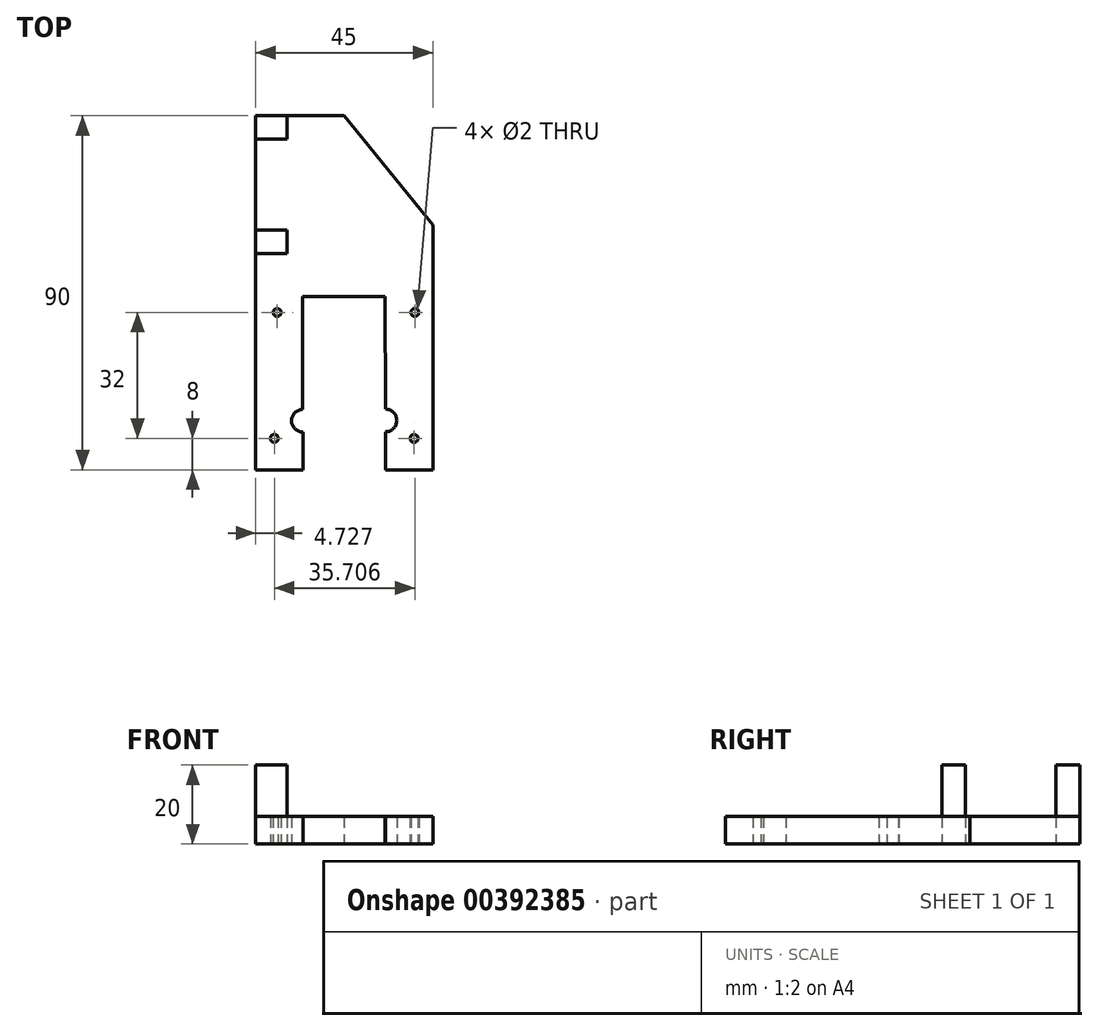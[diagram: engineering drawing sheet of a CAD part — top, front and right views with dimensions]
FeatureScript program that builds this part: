
annotation { "Feature Type Name" : "Feature", "Feature Type Description" : "" }
export const myFeature = defineFeature(function(context is Context, id is Id, definition is map)
    precondition{}
    {
        {
            var Q0;
            Q0=qCreatedBy(makeId("Top.planeOp"),FACE);
            var sketch = newSketch(context, id + "F0", { "sketchPlane" : qUnion([Q0])});
            skLineSegment(sketch, "E0.bottom", {"start": v(22.5, -45) * mm, "end": v(10.5, -45) * mm});
            skLineSegment(sketch, "E0.top", {"start": v(22.5, 45) * mm, "end": v(-22.5, 45) * mm});
            skLineSegment(sketch, "E0.left", {"start": v(22.5, -45) * mm, "end": v(22.5, 45) * mm});
            skLineSegment(sketch, "E0.right", {"start": v(-22.5, -45) * mm, "end": v(-22.5, 45) * mm});
            skPoint(sketch, "E0.middle", {"position": v(0, 0) * mm});
            skLineSegment(sketch, "E1.bottom", {"start": v(-10.63, -1) * mm, "end": v(10.37, -0.94) * mm});
            skLineSegment(sketch, "E1.left", {"start": v(-10.63, -1) * mm, "end": v(-10.5, -45) * mm});
            skLineSegment(sketch, "E1.right", {"start": v(10.37, -0.94) * mm, "end": v(10.5, -45) * mm});
            skLineSegment(sketch, "E2.bottom", {"start": v(-22.5, 39) * mm, "end": v(-14.5, 39) * mm});
            skLineSegment(sketch, "E2.top", {"start": v(-22.5, 45) * mm, "end": v(-14.5, 45) * mm});
            skLineSegment(sketch, "E2.left", {"start": v(-22.5, 39) * mm, "end": v(-22.5, 45) * mm});
            skLineSegment(sketch, "E2.right", {"start": v(-14.5, 39) * mm, "end": v(-14.5, 45) * mm});
            skLineSegment(sketch, "E3.bottom", {"start": v(-22.5, 16) * mm, "end": v(-14.5, 16) * mm});
            skLineSegment(sketch, "E3.top", {"start": v(-22.5, 10) * mm, "end": v(-14.5, 10) * mm});
            skLineSegment(sketch, "E3.left", {"start": v(-22.5, 16) * mm, "end": v(-22.5, 10) * mm});
            skLineSegment(sketch, "E3.right", {"start": v(-14.5, 16) * mm, "end": v(-14.5, 10) * mm});
            skLineSegment(sketch, "E4.trimOffspring", {"start": v(-10.5, -45) * mm, "end": v(-22.5, -45) * mm});
            skPoint(sketch, "E5", {"position": v(-17.77, -37) * mm});
            skPoint(sketch, "E6", {"position": v(-17.07, -5) * mm});
            skPoint(sketch, "E7", {"position": v(17.93, -5) * mm});
            skPoint(sketch, "E8", {"position": v(17.73, -37) * mm});
            skPoint(sketch, "E9.positionSnap0", {"position": v(-18.5, 45) * mm});
            skPoint(sketch, "E10.positionSnap0", {"position": v(-18.5, 16) * mm});
            skPoint(sketch, "E11", {"position": v(-10.54, -32.5) * mm});
            skPoint(sketch, "E12", {"position": v(0, 45) * mm});
            skPoint(sketch, "E13", {"position": v(22.5, 17.15) * mm});
            skLineSegment(sketch, "E14", {"start": v(0, 45) * mm, "end": v(22.5, 17.15) * mm});
            skPoint(sketch, "E15", {"position": v(10.46, -32.44) * mm});
            skLineSegment(sketch, "E16", {"start": v(0, -64.42) * mm, "end": v(0, 71.46) * mm, "construction": true});
            skSolve(sketch);
        }
        {
            var Q0;
            Q0=makeQuery(id+"F0.imprint","IMPRINT",FACE,{"disambiguationData":[TD([[makeQuery(id+"F0.imprint","IMPRINT",EDGE,{"derivedFrom":sQuery(id+"F0.wireOp",EDGE,"E2.bottom")}),1.0]])]});
            extrude(context, id + "F1", {"entities" : qUnion([Q0]), "depth" : 20 * mm});
        }
        {
            var Q0;
            Q0=makeQuery(id+"F0.imprint","IMPRINT",FACE,{"disambiguationData":[TD([[makeQuery(id+"F0.imprint","IMPRINT",EDGE,{"derivedFrom":sQuery(id+"F0.wireOp",EDGE,"E3.bottom")}),-1.0]])]});
            extrude(context, id + "F2", {"entities" : qUnion([Q0]), "depth" : 20 * mm});
        }
        {
            var Q0;
            Q0=makeQuery(id+"F0.imprint","IMPRINT",FACE,{"disambiguationData":[TD([[makeQuery(id+"F0.imprint","IMPRINT",EDGE,{"derivedFrom":sQuery(id+"F0.wireOp",EDGE,"E0.bottom")}),-1.0]])]});
            extrude(context, id + "F3", {"entities" : qUnion([Q0]), "depth" : 7 * mm});
        }
        {
            var Q0;
            Q0=sQuery(id+"F0.wireOp",VERTEX,"E6");
            var Q1;
            Q1=sQuery(id+"F0.wireOp",VERTEX,"E5");
            var Q2;
            Q2=sQuery(id+"F0.wireOp",VERTEX,"E8");
            var Q3;
            Q3=sQuery(id+"F0.wireOp",VERTEX,"E7");
            var Q4;
            Q4=makeQuery(id+"F3.opExtrude","SWEPT_BODY",BODY,{"disambiguationData":[OSD([sQuery(id+"F0.wireOp",EDGE,"E0.bottom"),sQuery(id+"F0.wireOp",EDGE,"E0.top"),sQuery(id+"F0.wireOp",EDGE,"E0.left"),sQuery(id+"F0.wireOp",EDGE,"E0.right"),sQuery(id+"F0.wireOp",EDGE,"E1.bottom"),sQuery(id+"F0.wireOp",EDGE,"E1.left"),sQuery(id+"F0.wireOp",EDGE,"E1.right"),sQuery(id+"F0.wireOp",EDGE,"E2.bottom"),sQuery(id+"F0.wireOp",EDGE,"E2.right"),sQuery(id+"F0.wireOp",EDGE,"E3.bottom"),sQuery(id+"F0.wireOp",EDGE,"E3.top"),sQuery(id+"F0.wireOp",EDGE,"E3.right"),sQuery(id+"F0.wireOp",EDGE,"E4.trimOffspring")])]});
            hole(context, id + "F4", {"style" : HoleStyle.SIMPLE, "endStyle" : HoleEndStyle.THROUGH, "oppositeDirection" : true, "holeDiameter" : 2 * mm, "isTappedThrough" : true, "tappedDepth" : 12.7 * mm, "tapClearance" : 3, "locations" : qUnion([Q0, Q1, Q2, Q3]), "scope" : qUnion([Q4])});
        }
        {
            var Q0;
            Q0=sQuery(id+"F0.wireOp",VERTEX,"E11");
            var Q1;
            Q1=sQuery(id+"F0.wireOp",VERTEX,"E15");
            var Q2;
            Q2=makeQuery(id+"F3.opExtrude","SWEPT_BODY",BODY,{"disambiguationData":[OSD([sQuery(id+"F0.wireOp",EDGE,"E0.bottom"),sQuery(id+"F0.wireOp",EDGE,"E0.top"),sQuery(id+"F0.wireOp",EDGE,"E0.left"),sQuery(id+"F0.wireOp",EDGE,"E0.right"),sQuery(id+"F0.wireOp",EDGE,"E1.bottom"),sQuery(id+"F0.wireOp",EDGE,"E1.left"),sQuery(id+"F0.wireOp",EDGE,"E1.right"),sQuery(id+"F0.wireOp",EDGE,"E2.bottom"),sQuery(id+"F0.wireOp",EDGE,"E2.right"),sQuery(id+"F0.wireOp",EDGE,"E3.bottom"),sQuery(id+"F0.wireOp",EDGE,"E3.top"),sQuery(id+"F0.wireOp",EDGE,"E3.right"),sQuery(id+"F0.wireOp",EDGE,"E4.trimOffspring")])]});
            hole(context, id + "F5", {"style" : HoleStyle.SIMPLE, "endStyle" : HoleEndStyle.THROUGH, "oppositeDirection" : true, "holeDiameter" : 5.75 * mm, "isTappedThrough" : true, "tappedDepth" : 12.7 * mm, "tapClearance" : 3, "locations" : qUnion([Q0, Q1]), "scope" : qUnion([Q2])});
        }
    });
